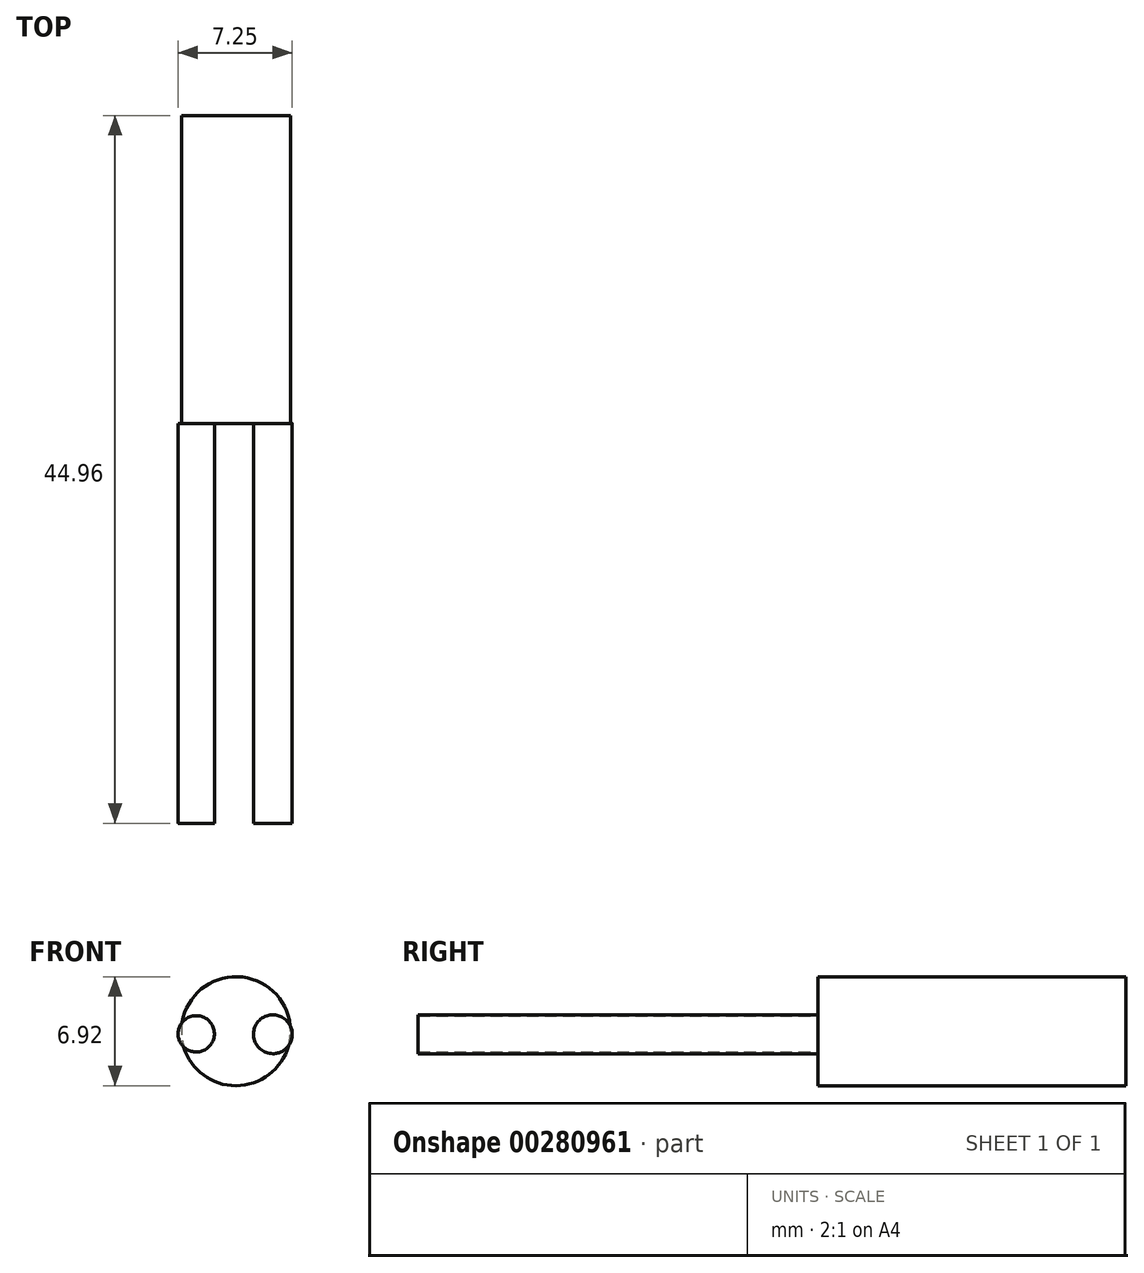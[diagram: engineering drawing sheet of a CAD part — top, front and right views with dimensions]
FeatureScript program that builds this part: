
annotation { "Feature Type Name" : "Feature", "Feature Type Description" : "" }
export const myFeature = defineFeature(function(context is Context, id is Id, definition is map)
    precondition{}
    {
        {
            var Q0;
            Q0=qCreatedBy(makeId("Front.planeOp"),FACE);
            var sketch = newSketch(context, id + "F0", { "sketchPlane" : qUnion([Q0])});
            skCircle(sketch, "E0", {"center": v(-52.23, 16.55) * mm, "radius": 3.46 * mm});
            skSolve(sketch);
        }
        {
            var Q0;
            Q0=makeQuery(id+"F0.imprint","IMPRINT",FACE,{"disambiguationData":[TD([[makeQuery(id+"F0.imprint","IMPRINT",EDGE,{"derivedFrom":sQuery(id+"F0.wireOp",EDGE,"E0")}),1.0]])]});
            extrude(context, id + "F1", {"entities" : qUnion([Q0]), "oppositeDirection" : true, "depth" : 19.56 * mm});
        }
        {
            var Q0;
            Q0=qCreatedBy(makeId("Front.planeOp"),FACE);
            var sketch = newSketch(context, id + "F2", { "sketchPlane" : qUnion([Q0])});
            skCircle(sketch, "E1", {"center": v(-54.75, 16.38) * mm, "radius": 1.15 * mm});
            skCircle(sketch, "E2", {"center": v(-49.88, 16.35) * mm, "radius": 1.23 * mm});
            skSolve(sketch);
        }
        {
            var Q0;
            Q0=makeQuery(id+"F2.imprint","IMPRINT",FACE,{"disambiguationData":[TD([[makeQuery(id+"F2.imprint","IMPRINT",EDGE,{"derivedFrom":sQuery(id+"F2.wireOp",EDGE,"E1")}),1.0]])]});
            extrude(context, id + "F3", {"entities" : qUnion([Q0]), "operationType" : NewBodyOperationType.ADD, "depth" : 25.4 * mm});
        }
        {
            var Q0;
            Q0=makeQuery(id+"F2.imprint","IMPRINT",FACE,{"disambiguationData":[TD([[makeQuery(id+"F2.imprint","IMPRINT",EDGE,{"derivedFrom":sQuery(id+"F2.wireOp",EDGE,"E2")}),1.0]])]});
            extrude(context, id + "F4", {"entities" : qUnion([Q0]), "operationType" : NewBodyOperationType.ADD, "depth" : 25.4 * mm});
        }
    });
